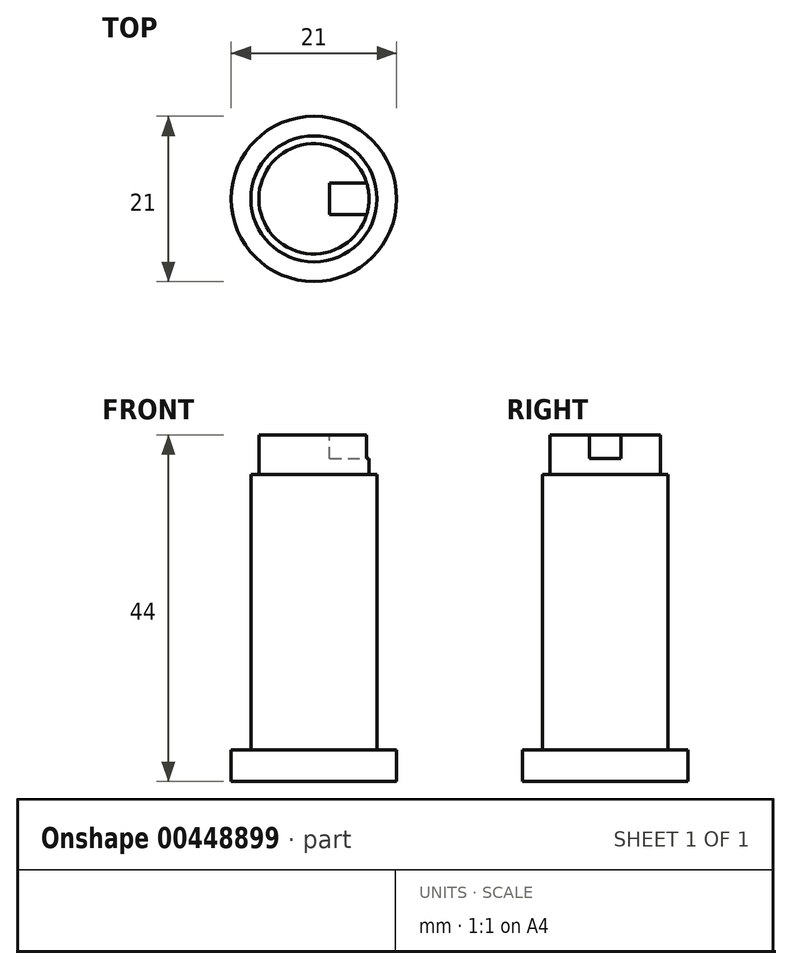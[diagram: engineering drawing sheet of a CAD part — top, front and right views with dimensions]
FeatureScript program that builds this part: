
annotation { "Feature Type Name" : "Feature", "Feature Type Description" : "" }
export const myFeature = defineFeature(function(context is Context, id is Id, definition is map)
    precondition{}
    {
        {
            var Q0;
            Q0=qCreatedBy(makeId("Top.planeOp"),FACE);
            var sketch = newSketch(context, id + "F0", { "sketchPlane" : qUnion([Q0])});
            skCircle(sketch, "E0", {"center": v(0, 0) * mm, "radius": 10.5 * mm});
            skSolve(sketch);
        }
        {
            var Q0;
            Q0=qSketchRegion(id+"F0",true);
            extrude(context, id + "F1", {"entities" : qUnion([Q0]), "depth" : 4 * mm});
        }
        {
            var Q0;
            Q0=qCreatedBy(makeId("Top.planeOp"),FACE);
            var sketch = newSketch(context, id + "F2", { "sketchPlane" : qUnion([Q0])});
            skCircle(sketch, "E1", {"center": v(0, 0) * mm, "radius": 8 * mm});
            skSolve(sketch);
        }
        {
            var Q0;
            Q0=qSketchRegion(id+"F2",true);
            extrude(context, id + "F3", {"entities" : qUnion([Q0]), "operationType" : NewBodyOperationType.ADD, "depth" : 39 * mm});
        }
        {
            var Q0;
            Q0=qCreatedBy(makeId("Right.planeOp"),FACE);
            var sketch = newSketch(context, id + "F4", { "sketchPlane" : qUnion([Q0])});
            skLineSegment(sketch, "E2", {"start": v(0, 44) * mm, "end": v(0, 39) * mm});
            skLineSegment(sketch, "E3", {"start": v(0, 39) * mm, "end": v(7, 39) * mm});
            skLineSegment(sketch, "E4", {"start": v(7, 39) * mm, "end": v(7, 44) * mm});
            skLineSegment(sketch, "E5", {"start": v(7, 44) * mm, "end": v(0, 44) * mm});
            skSolve(sketch);
        }
        {
            var Q0;
            Q0=makeQuery(id+"F4.imprint","IMPRINT",FACE,{"disambiguationData":[TD([[makeQuery(id+"F4.imprint","IMPRINT",EDGE,{"derivedFrom":sQuery(id+"F4.wireOp",EDGE,"E2")}),1.0]])]});
            var Q1;
            Q1=sQuery(id+"F4.wireOp",EDGE,"E2");
            revolve(context, id + "F5", {"operationType" : NewBodyOperationType.ADD, "entities" : qUnion([Q0]), "axis" : qUnion([Q1]), "revolveType" : RevolveType.FULL});
        }
        {
            var Q0;
            Q0=makeQuery(id+"F5.opRevolve","SWEPT_FACE",FACE,{"disambiguationData":[OSD([sQuery(id+"F4.wireOp",EDGE,"E5")])]});
            var sketch = newSketch(context, id + "F6", { "sketchPlane" : qUnion([Q0])});
            skLineSegment(sketch, "E6.bottom", {"start": v(2, 2) * mm, "end": v(9.26, 2) * mm});
            skLineSegment(sketch, "E6.top", {"start": v(2, -2) * mm, "end": v(9.26, -2) * mm});
            skLineSegment(sketch, "E6.left", {"start": v(2, 2) * mm, "end": v(2, -2) * mm});
            skLineSegment(sketch, "E6.right", {"start": v(9.26, 2) * mm, "end": v(9.26, -2) * mm});
            skSolve(sketch);
        }
        {
            var Q0;
            {var subQ0=sQuery(id+"F6.wireOp",EDGE,"E6.left");Q0=makeQuery(id+"F6.imprint","IMPRINT",FACE,{"disambiguationData":[TD([[makeQuery(id+"F6.imprint","IMPRINT",EDGE,{"derivedFrom":subQ0}),1.0]])]});}
            extrude(context, id + "F7", {"entities" : qUnion([Q0]), "operationType" : NewBodyOperationType.REMOVE, "oppositeDirection" : true, "depth" : 3 * mm});
        }
    });
